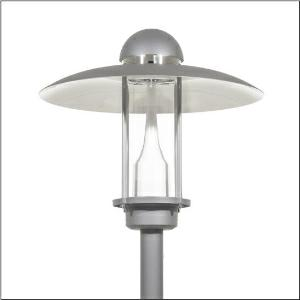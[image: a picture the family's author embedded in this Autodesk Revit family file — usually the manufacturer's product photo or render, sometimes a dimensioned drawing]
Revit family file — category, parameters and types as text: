
# Revit family: city-light_elegance_iq___st1_2a_5xa5265af14h_1cc4
name_source: partatom
category: Lighting Fixtures
units: mm (PartAtom-declared; Revit-internal decimal feet)

## family parameters
Cut with Voids When Loaded = No
Host = Face
Light Source = No
Part Type = Normal
Room Calculation Point = No
Round Connector Dimension = Use Diameter
Shared = No

## types (1)
- --- (1 x LED, 1470 lm, 12.9 W, 2200K)
    Apparent Load = 13 VA
    CIE Flux Codes = 22 62 94 98 100
    Color Rendering = 70
    Color Temperature = 2200K
    Default Elevation = 1800 mm
    Description = City-Light Elegance iQ, mast luminaire, Module 540 iQ-SR, primary light control with 3 zone facetted reflector, of plastic, silver coated, highly specular, structured, primary optical cover: cover, of PMMA, transparent, light distribution: ST1.2a, light emission: direct distribution, primary light characteristic: asymmetric, installation type: post-top, LED, High Power LED, rated luminous flux: 1.470lm, luminous efficacy: 114lm/W, light colour: 722, colour temperature: 2200K, control gear: ECG iQ, control: presetting dimming logarithmic, Street-Remote, Auto-Match, Temp-Guard, Lumen-Switch, Night-Set, Smart-Wire, Light-Fading, Desk-Remote (wireless, voltage-free reading and setting of iQ features in the workshop via application-optimized NFC function/RFID function), optimised constant luminous flux control (CLO 2.0), with terminal, 6-pole, max. 2.5mm², mains connection: 230..240V, AC, 50/60Hz, start of lifetime: 13W, end of service life: 13W, reduction: 6W, luminaire housing, upper part, of aluminium, coated, Siteco® metallic grey (DB 702S), diameter: 750mm, height: 675mm, spigot size: d x l = 76 x 70mm (post-top) | with reducer (optional accessory) 60 x 70mm, post-top mast mounting element, of diecast aluminium, coated, Siteco® metallic grey (DB 702S), Module 540 iQ-SR, traffic white (RAL 9016), equipment: standard, protection rating (complete): IP65, insulation class (complete): insulation class II (safety insulation), certification: CE, ENEC, VDE, packaging unit: 1 piece

Light Distribution: ST1.2a
    Height = 675 mm
    Lamp = 1 x LED
    Lamp Light Flux = 1470 lm
    Lamp Power = 12.9 W
    Lamp count = 1
    Length = 750 mm
    Luminous efficacy = 114 lm/W
    Manufacturer = Siteco
    ModVariant = No
    Model = 5XA5265AF14H
    Number of Poles = 1
    OnlyDefault = Yes
    Power Factor = 1
    Product Name = City-Light Elegance iQ | ST1.2a
    Product group = mast luminaire | pylon top
    ProductGroupID = 6100
    Protection Class = Protection class II
    Protection Degree = IP 65
    RLX_Detail_Level = 1
    RLX_Emergency_Light_Flux = 0 lm
    RLX_Emergency_Type = 0
    RLX_Emergency_Type_DB = No
    RlxData = <blob elided: 100085 chars, md5=ef0afc1a>
    Socket = socket
    Standby Power = 0 W
    System Light Flux = 1470 lm
    System Power = 13 W
    Type Comments = factory setting: luminous flux: 100 % | dim-lin: 254 | 516 mA
    Type Image = l_1006912.jpg
    URL = http://relux.com
    VarID = @adj_092211
    Voltage = 0 V
    Weight = 0.00 kg
    Width = 0 mm  [stored 0 ft]

note: [stored X ft] marks values corroborated as IEEE doubles in the binary element streams (Revit-internal decimal feet)

## geometry (parser evidence)
native form markers: Blend x4, Sweep x11
no freeform markers — native parametric forms only
